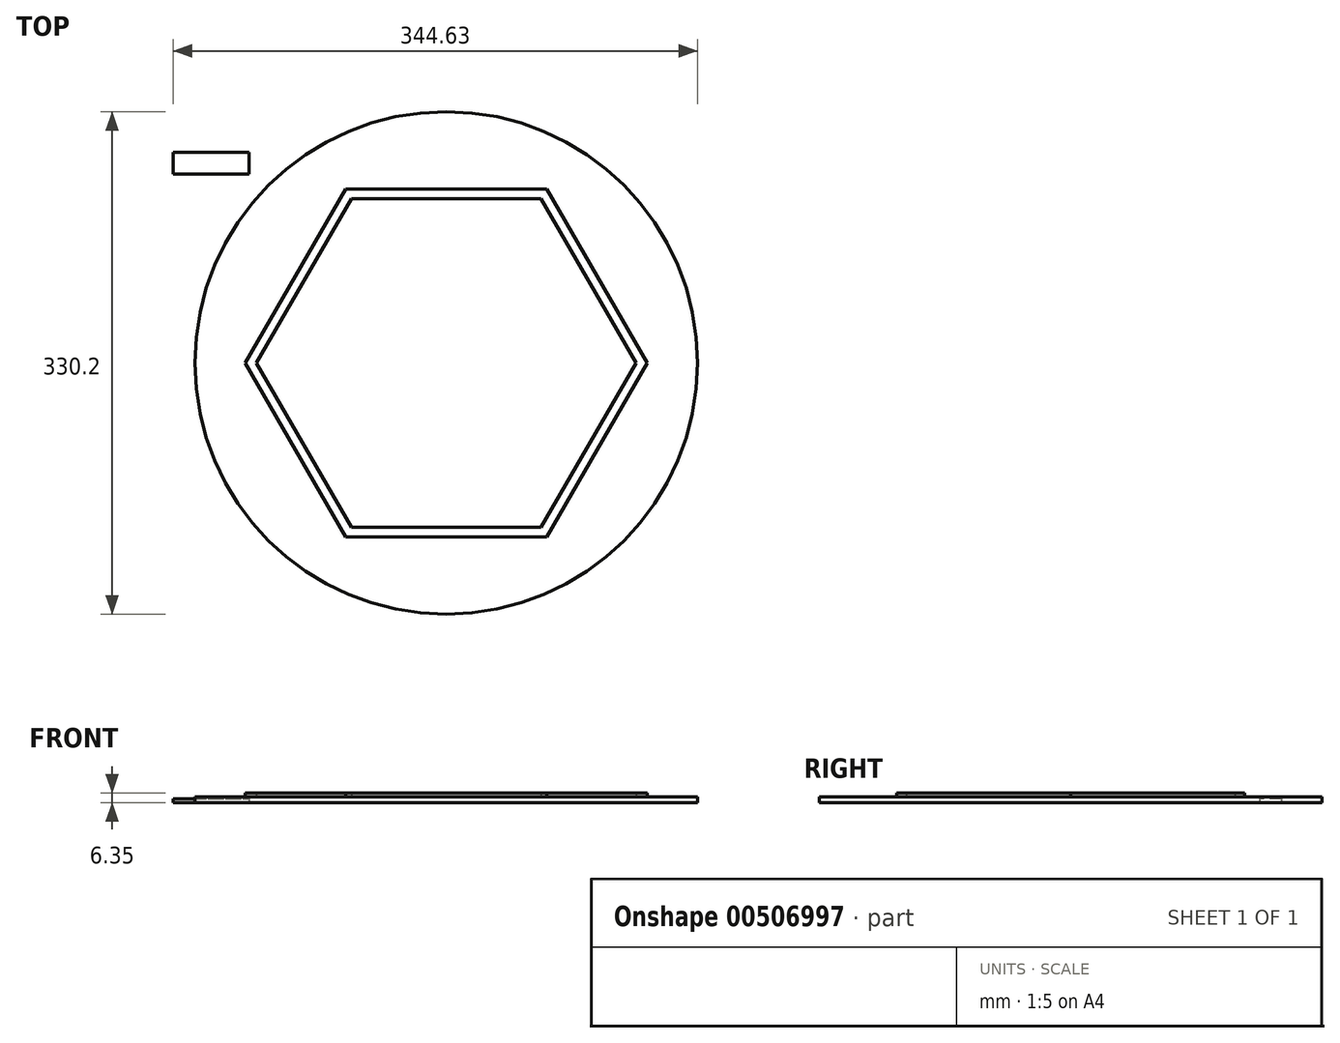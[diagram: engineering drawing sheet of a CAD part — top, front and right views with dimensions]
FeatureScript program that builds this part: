
annotation { "Feature Type Name" : "Feature", "Feature Type Description" : "" }
export const myFeature = defineFeature(function(context is Context, id is Id, definition is map)
    precondition{}
    {
        {
            var Q0;
            Q0=qCreatedBy(makeId("Top.planeOp"),FACE);
            var sketch = newSketch(context, id + "F0", { "sketchPlane" : qUnion([Q0])});
            skCircle(sketch, "E0", {"center": v(0, 0) * mm, "radius": 165.1 * mm});
            skCircle(sketch, "E1.cCircle", {"center": v(0, 0) * mm, "radius": 114.3 * mm, "construction": true});
            skLineSegment(sketch, "E1.0", {"start": v(-131.98, 0) * mm, "end": v(-66, 114.3) * mm});
            skLineSegment(sketch, "E1.1", {"start": v(-66, 114.3) * mm, "end": v(66, 114.3) * mm});
            skLineSegment(sketch, "E1.2", {"start": v(66, 114.3) * mm, "end": v(131.98, 0) * mm});
            skLineSegment(sketch, "E1.3", {"start": v(131.98, 0) * mm, "end": v(66, -114.3) * mm});
            skLineSegment(sketch, "E1.4", {"start": v(66, -114.3) * mm, "end": v(-66, -114.3) * mm});
            skLineSegment(sketch, "E1.5", {"start": v(-66, -114.3) * mm, "end": v(-131.98, 0) * mm});
            skPoint(sketch, "E1.0.midPoint", {"position": v(-98.99, 57.15) * mm});
            skLineSegment(sketch, "E2.0", {"start": v(-124.65, 0) * mm, "end": v(-62.32, 107.95) * mm});
            skLineSegment(sketch, "E2.1", {"start": v(62.32, 107.95) * mm, "end": v(124.65, 0) * mm});
            skLineSegment(sketch, "E2.2", {"start": v(124.65, 0) * mm, "end": v(62.32, -107.95) * mm});
            skLineSegment(sketch, "E2.3", {"start": v(-62.32, 107.95) * mm, "end": v(62.32, 107.95) * mm});
            skLineSegment(sketch, "E2.4", {"start": v(62.32, -107.95) * mm, "end": v(-62.32, -107.95) * mm});
            skLineSegment(sketch, "E2.5", {"start": v(-62.32, -107.95) * mm, "end": v(-124.65, 0) * mm});
            skSolve(sketch);
        }
        {
            var Q0;
            Q0=makeQuery(id+"F0.imprint","IMPRINT",FACE,{"disambiguationData":[TD([[makeQuery(id+"F0.imprint","IMPRINT",EDGE,{"derivedFrom":sQuery(id+"F0.wireOp",EDGE,"E0")}),1.0]])]});
            var sketch = newSketch(context, id + "F1", { "sketchPlane" : qUnion([Q0])});
            skLineSegment(sketch, "E3.bottom", {"start": v(-179.53, 138.38) * mm, "end": v(-129.53, 138.38) * mm});
            skLineSegment(sketch, "E3.top", {"start": v(-179.53, 124.18) * mm, "end": v(-129.53, 124.18) * mm});
            skLineSegment(sketch, "E3.left", {"start": v(-179.53, 138.38) * mm, "end": v(-179.53, 124.18) * mm});
            skLineSegment(sketch, "E3.right", {"start": v(-129.53, 138.38) * mm, "end": v(-129.53, 124.18) * mm});
            skSolve(sketch);
        }
        {
            var Q0;
            Q0=makeQuery(id+"F0.imprint","IMPRINT",FACE,{"disambiguationData":[TD([[makeQuery(id+"F0.imprint","IMPRINT",EDGE,{"derivedFrom":sQuery(id+"F0.wireOp",EDGE,"E0")}),1.0]])]});
            var Q1;
            Q1=makeQuery(id+"F0.imprint","IMPRINT",FACE,{"disambiguationData":[TD([[makeQuery(id+"F0.imprint","IMPRINT",EDGE,{"derivedFrom":sQuery(id+"F0.wireOp",EDGE,"E2.0")}),-1.0]])]});
            var Q2;
            Q2=makeQuery(id+"F0.imprint","IMPRINT",FACE,{"disambiguationData":[TD([[makeQuery(id+"F0.imprint","IMPRINT",EDGE,{"derivedFrom":sQuery(id+"F0.wireOp",EDGE,"E1.0")}),-1.0]])]});
            extrude(context, id + "F2", {"entities" : qUnion([Q0, Q1, Q2]), "depth" : 3.8 * mm, "offsetDistance" : 25.4 * mm});
        }
        {
            var Q0;
            Q0=makeQuery(id+"F1.imprint","IMPRINT",FACE,{"disambiguationData":[TD([[makeQuery(id+"F1.imprint","IMPRINT",EDGE,{"derivedFrom":sQuery(id+"F1.wireOp",EDGE,"E3.bottom")}),-1.0]])]});
            extrude(context, id + "F3", {"entities" : qUnion([Q0]), "depth" : 2.54 * mm, "offsetDistance" : 25.4 * mm});
        }
        {
            var Q0;
            Q0=makeQuery(id+"F2.opExtrude","CAP_FACE",FACE,{"disambiguationData":[OSD([sQuery(id+"F0.wireOp",EDGE,"E0")])],"isStart":false});
            var sketch = newSketch(context, id + "F4", { "sketchPlane" : qUnion([Q0])});
            skLineSegment(sketch, "E4.0", {"start": v(-131.98, 0) * mm, "end": v(-66, 114.3) * mm});
            skLineSegment(sketch, "E5.0", {"start": v(-124.65, 0) * mm, "end": v(-62.32, 107.95) * mm});
            skLineSegment(sketch, "E6.0", {"start": v(-62.32, 107.95) * mm, "end": v(62.32, 107.95) * mm});
            skLineSegment(sketch, "E7.0", {"start": v(-66, 114.3) * mm, "end": v(66, 114.3) * mm});
            skLineSegment(sketch, "E8.0", {"start": v(-66, -114.3) * mm, "end": v(-131.98, 0) * mm});
            skLineSegment(sketch, "E9.0", {"start": v(-62.32, -107.95) * mm, "end": v(-124.65, 0) * mm});
            skLineSegment(sketch, "E10.0", {"start": v(62.32, -107.95) * mm, "end": v(-62.32, -107.95) * mm});
            skLineSegment(sketch, "E11.0", {"start": v(66, -114.3) * mm, "end": v(-66, -114.3) * mm});
            skLineSegment(sketch, "E12.0", {"start": v(124.65, 0) * mm, "end": v(62.32, -107.95) * mm});
            skLineSegment(sketch, "E13.0", {"start": v(131.98, 0) * mm, "end": v(66, -114.3) * mm});
            skLineSegment(sketch, "E14.0", {"start": v(62.32, 107.95) * mm, "end": v(124.65, 0) * mm});
            skLineSegment(sketch, "E15.0", {"start": v(66, 114.3) * mm, "end": v(131.98, 0) * mm});
            skSolve(sketch);
        }
        {
            var Q0;
            Q0=makeQuery(id+"F4.imprint","IMPRINT",FACE,{"disambiguationData":[TD([[makeQuery(id+"F4.imprint","IMPRINT",EDGE,{"derivedFrom":sQuery(id+"F4.wireOp",EDGE,"E4.0")}),-1.0]])]});
            extrude(context, id + "F5", {"entities" : qUnion([Q0]), "operationType" : NewBodyOperationType.ADD, "depth" : 2.54 * mm, "offsetDistance" : 25.4 * mm});
        }
    });
